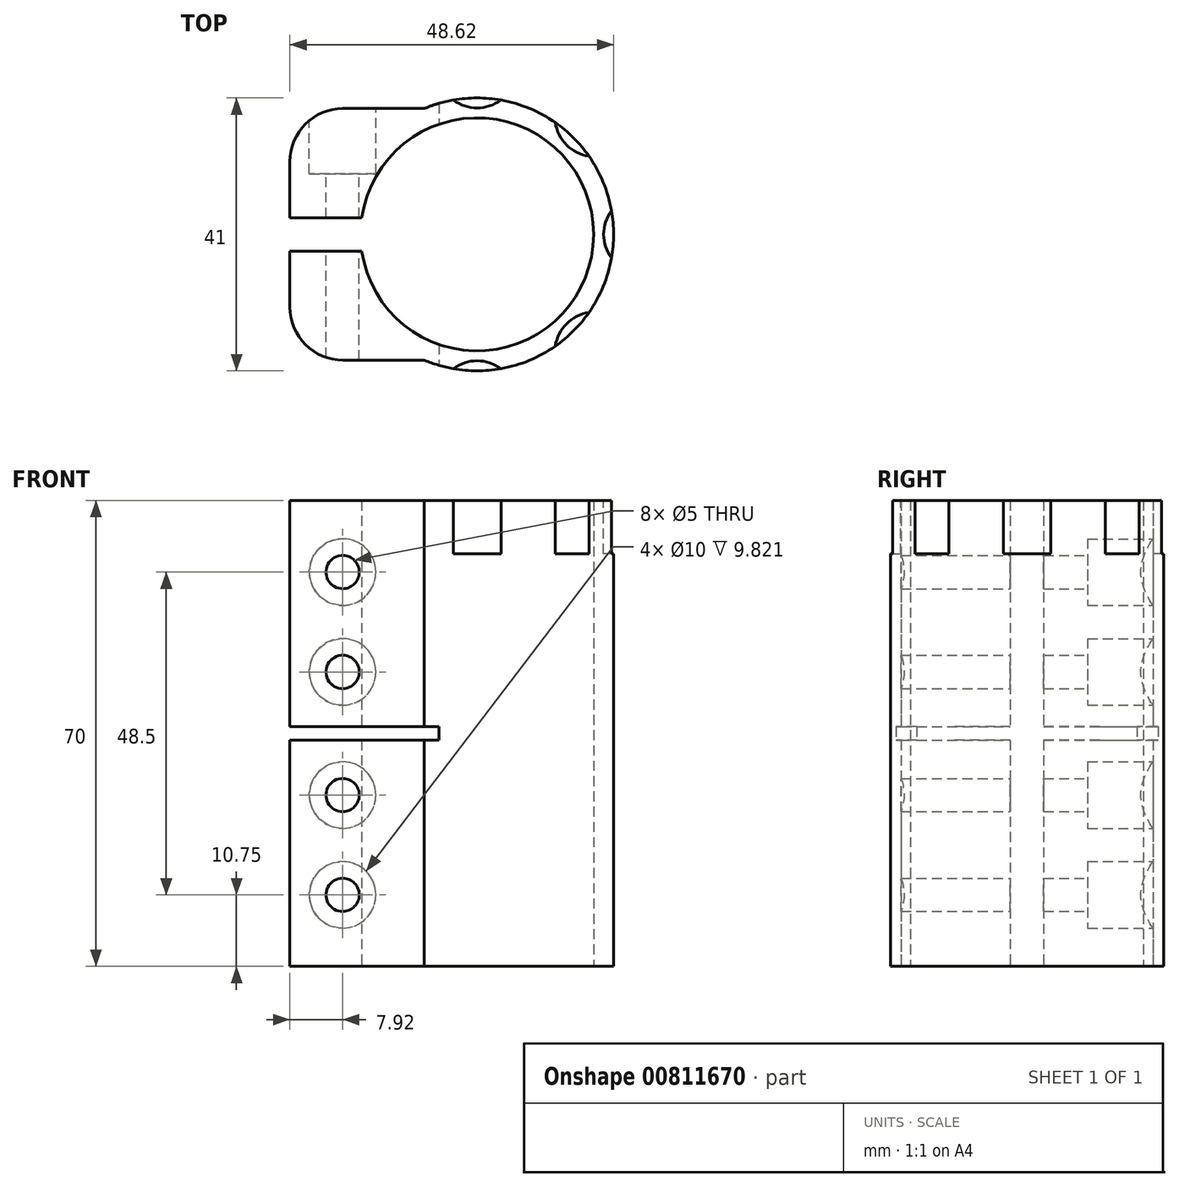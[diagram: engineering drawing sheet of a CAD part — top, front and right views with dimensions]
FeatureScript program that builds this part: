
annotation { "Feature Type Name" : "Feature", "Feature Type Description" : "" }
export const myFeature = defineFeature(function(context is Context, id is Id, definition is map)
    precondition{}
    {
        {
            var Q0;
            Q0=qCreatedBy(makeId("Top.planeOp"),FACE);
            var sketch = newSketch(context, id + "F0", { "sketchPlane" : qUnion([Q0])});
            skArc(sketch, "E0", {"start": v(-7.92, -18.9) * mm, "mid": v(20.5, 0) * mm, "end": v(-7.92, 18.9) * mm});
            skCircle(sketch, "E1", {"center": v(0, 0) * mm, "radius": 17.5 * mm});
            skLineSegment(sketch, "E2", {"start": v(-7.92, 18.9) * mm, "end": v(-20.12, 18.9) * mm});
            skLineSegment(sketch, "E3", {"start": v(-17.32, 2.5) * mm, "end": v(-28.12, 2.5) * mm});
            skLineSegment(sketch, "E4", {"start": v(-28.12, 2.5) * mm, "end": v(-28.12, 10.9) * mm});
            skPoint(sketch, "E5.visualSharp", {"position": v(-28.12, 18.9) * mm});
            skArc(sketch, "E5.filletArc", {"start": v(-20.12, 18.9) * mm, "mid": v(-25.78, 16.57) * mm, "end": v(-28.12, 10.9) * mm});
            skLineSegment(sketch, "E6", {"start": v(41.34, 0) * mm, "end": v(0, 0) * mm, "construction": true});
            skLineSegment(sketch, "E7.MirrorCS", {"start": v(-28.12, -2.5) * mm, "end": v(-28.12, -10.9) * mm});
            skLineSegment(sketch, "E8.MirrorCS", {"start": v(-7.92, -18.9) * mm, "end": v(-20.12, -18.9) * mm});
            skLineSegment(sketch, "E9.MirrorCS", {"start": v(-17.32, -2.5) * mm, "end": v(-28.12, -2.5) * mm});
            skArc(sketch, "E10.MirrorCS", {"start": v(-20.12, -18.9) * mm, "mid": v(-25.78, -16.57) * mm, "end": v(-28.12, -10.9) * mm});
            skPoint(sketch, "E11.orphan", {"position": v(-17.32, -2.5) * mm});
            skPoint(sketch, "E12.orphan", {"position": v(-17.32, 2.5) * mm});
            skSolve(sketch);
        }
        {
            var Q0;
            Q0=makeQuery(id+"F0.imprint","IMPRINT",FACE,{"disambiguationData":[TD([[makeQuery(id+"F0.imprint","IMPRINT",EDGE,{"derivedFrom":sQuery(id+"F0.wireOp",EDGE,"E0")}),1.0]])]});
            extrude(context, id + "F1", {"entities" : qUnion([Q0]), "endBound" : BoundingType.SYMMETRIC, "depth" : 70 * mm, "offsetDistance" : 25 * mm});
        }
        {
            var Q0;
            Q0=makeQuery(id+"F1.opExtrude","SWEPT_FACE",FACE,{"disambiguationData":[OSD([sQuery(id+"F0.wireOp",EDGE,"E2")])]});
            var sketch = newSketch(context, id + "F2", { "sketchPlane" : qUnion([Q0])});
            skPoint(sketch, "E13", {"position": v(20.2, 24.25) * mm});
            skPoint(sketch, "E14", {"position": v(20.2, 9.25) * mm});
            skPoint(sketch, "E15", {"position": v(20.2, -9.25) * mm});
            skPoint(sketch, "E16", {"position": v(20.2, -24.25) * mm});
            skSolve(sketch);
        }
        {
            var Q0;
            Q0=sQuery(id+"F2.wireOp",VERTEX,"E16");
            var Q1;
            Q1=sQuery(id+"F2.wireOp",VERTEX,"E15");
            var Q2;
            Q2=sQuery(id+"F2.wireOp",VERTEX,"E14");
            var Q3;
            Q3=sQuery(id+"F2.wireOp",VERTEX,"E13");
            var Q4;
            Q4=makeQuery(id+"F1.opExtrude","SWEPT_BODY",BODY,{"disambiguationData":[OSD([sQuery(id+"F0.wireOp",EDGE,"E0"),sQuery(id+"F0.wireOp",EDGE,"E1"),sQuery(id+"F0.wireOp",EDGE,"E2"),sQuery(id+"F0.wireOp",EDGE,"E3"),sQuery(id+"F0.wireOp",EDGE,"E4"),sQuery(id+"F0.wireOp",EDGE,"E5.filletArc"),sQuery(id+"F0.wireOp",EDGE,"E7.MirrorCS"),sQuery(id+"F0.wireOp",EDGE,"E8.MirrorCS"),sQuery(id+"F0.wireOp",EDGE,"E9.MirrorCS"),sQuery(id+"F0.wireOp",EDGE,"E10.MirrorCS")])]});
            hole(context, id + "F3", {"style" : HoleStyle.C_BORE, "endStyle" : HoleEndStyle.THROUGH, "holeDiameter" : 5 * mm, "cBoreDiameter" : 10 * mm, "cBoreDepth" : 8 * mm, "majorDiameter" : 5 * mm, "isTappedThrough" : true, "tappedDepth" : 12 * mm, "tapClearance" : 3, "locations" : qUnion([Q0, Q1, Q2, Q3]), "scope" : qUnion([Q4])});
        }
        {
            var Q0;
            Q0=qCreatedBy(makeId("Front.planeOp"),FACE);
            var sketch = newSketch(context, id + "F4", { "sketchPlane" : qUnion([Q0])});
            skLineSegment(sketch, "E17.bottom", {"start": v(-28.12, 1) * mm, "end": v(-5.72, 1) * mm});
            skLineSegment(sketch, "E17.top", {"start": v(-28.12, -1) * mm, "end": v(-5.72, -1) * mm});
            skLineSegment(sketch, "E17.left", {"start": v(-28.12, 1) * mm, "end": v(-28.12, -1) * mm});
            skLineSegment(sketch, "E17.right", {"start": v(-5.72, 1) * mm, "end": v(-5.72, -1) * mm});
            skSolve(sketch);
        }
        {
            var Q0;
            Q0 = qSketchRegion(id + "F4", true);
            extrude(context, id + "F5", {"entities" : qUnion([Q0]), "operationType" : NewBodyOperationType.REMOVE, "endBound" : BoundingType.SYMMETRIC, "oppositeDirection" : true, "depth" : 50 * mm, "offsetDistance" : 25 * mm});
        }
        {
            var Q0;
            Q0=makeQuery(id+"F1.opExtrude","CAP_FACE",FACE,{"disambiguationData":[OSD([sQuery(id+"F0.wireOp",EDGE,"E0"),sQuery(id+"F0.wireOp",EDGE,"E1"),sQuery(id+"F0.wireOp",EDGE,"E2"),sQuery(id+"F0.wireOp",EDGE,"E3"),sQuery(id+"F0.wireOp",EDGE,"E4"),sQuery(id+"F0.wireOp",EDGE,"E5.filletArc"),sQuery(id+"F0.wireOp",EDGE,"E7.MirrorCS"),sQuery(id+"F0.wireOp",EDGE,"E8.MirrorCS"),sQuery(id+"F0.wireOp",EDGE,"E9.MirrorCS"),sQuery(id+"F0.wireOp",EDGE,"E10.MirrorCS")])],"isStart":false});
            var sketch = newSketch(context, id + "F6", { "sketchPlane" : qUnion([Q0])});
            skCircle(sketch, "E18", {"center": v(0, -25) * mm, "radius": 6 * mm});
            skCircle(sketch, "E19.1.0", {"center": v(17.68, -17.68) * mm, "radius": 6 * mm});
            skCircle(sketch, "E19.2.0", {"center": v(25, 0) * mm, "radius": 6 * mm});
            skCircle(sketch, "E19.3.0", {"center": v(17.68, 17.68) * mm, "radius": 6 * mm});
            skCircle(sketch, "E19.4.0", {"center": v(0, 25) * mm, "radius": 6 * mm});
            skPoint(sketch, "E19.center", {"position": v(0, 0) * mm});
            skLineSegment(sketch, "E19.anchor1", {"start": v(0, 0) * mm, "end": v(0, -25) * mm, "construction": true});
            skLineSegment(sketch, "E19.anchor2", {"start": v(0, 0) * mm, "end": v(0, 25) * mm, "construction": true});
            skSolve(sketch);
        }
        {
            var Q0;
            Q0 = qSketchRegion(id + "F6", true);
            extrude(context, id + "F7", {"entities" : qUnion([Q0]), "operationType" : NewBodyOperationType.REMOVE, "oppositeDirection" : true, "depth" : 8 * mm, "offsetDistance" : 25 * mm});
        }
    });
